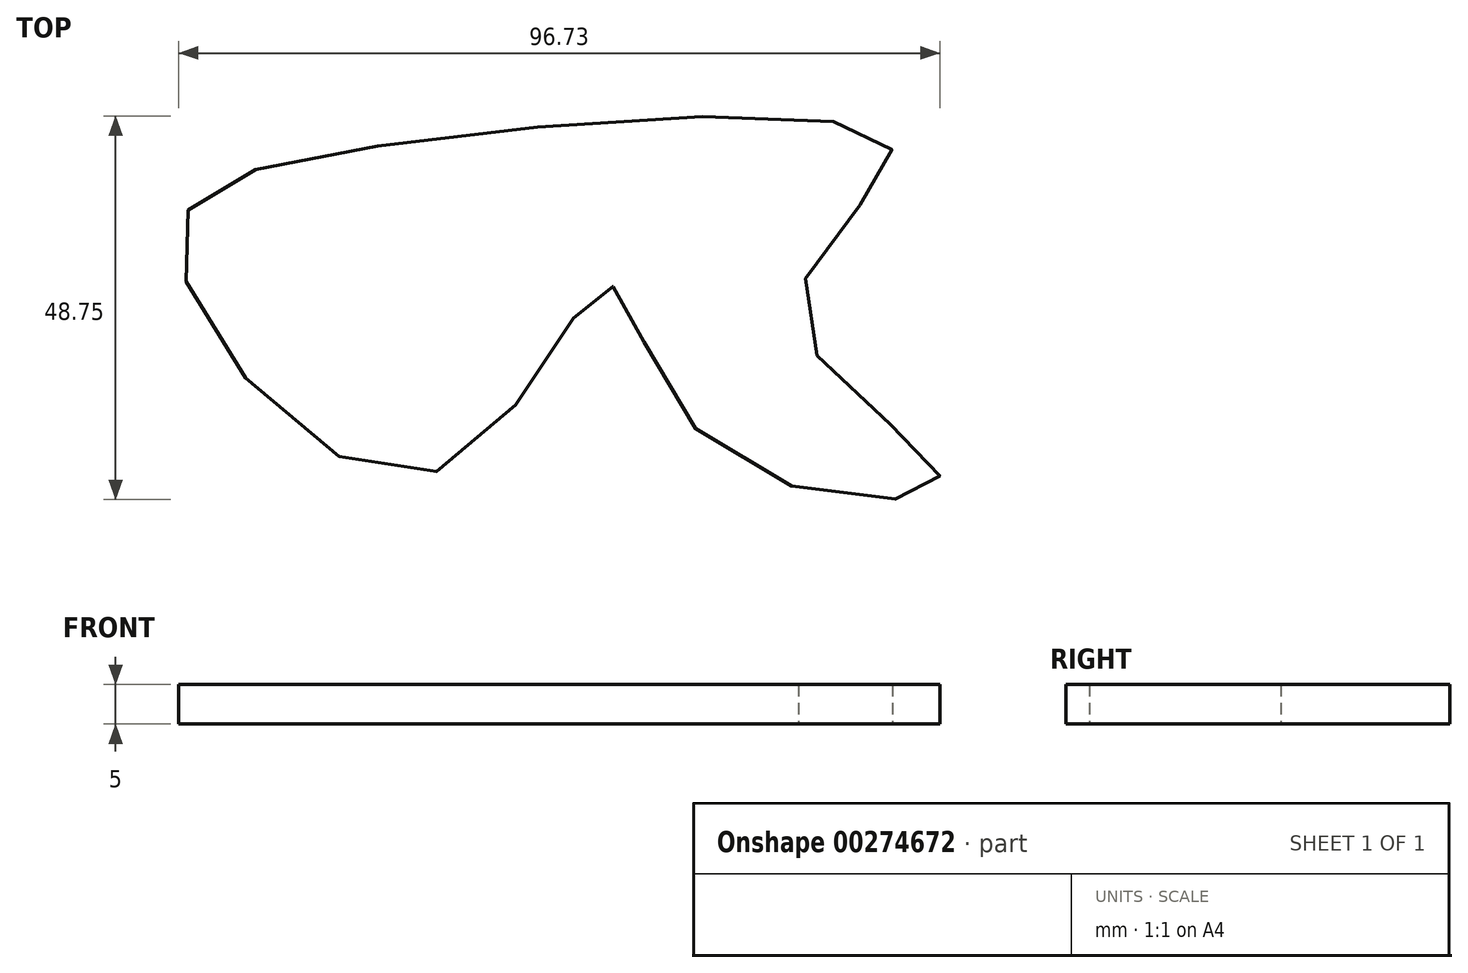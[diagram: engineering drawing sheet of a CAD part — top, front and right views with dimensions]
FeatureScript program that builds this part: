
annotation { "Feature Type Name" : "Feature", "Feature Type Description" : "" }
export const myFeature = defineFeature(function(context is Context, id is Id, definition is map)
    precondition{}
    {
        {
            var Q0;
            Q0=qCreatedBy(makeId("Top.planeOp"),FACE);
            var sketch = newSketch(context, id + "F0", { "sketchPlane" : qUnion([Q0])});
            skFitSpline(sketch, "E0", {"points": [v(-39.93, 47.31) * mm, v(25.46, 46.73) * mm, v(13.6, 25.9) * mm, v(31.54, 5.06) * mm, v(2.9, 9.12) * mm, v(-11, 29.66) * mm, v(-33.57, 5.64) * mm, v(-65.1, 33.71) * mm, v(-39.93, 47.31) * mm]});
            skSolve(sketch);
        }
        {
            var Q0;
            Q0=makeQuery(id+"F0.imprint","IMPRINT",FACE,{"disambiguationData":[TD([[makeQuery(id+"F0.imprint","IMPRINT",EDGE,{"derivedFrom":sQuery(id+"F0.wireOp",EDGE,"E0")}),-1.0]])]});
            extrude(context, id + "F1", {"entities" : qUnion([Q0]), "depth" : 5 * mm});
        }
    });
